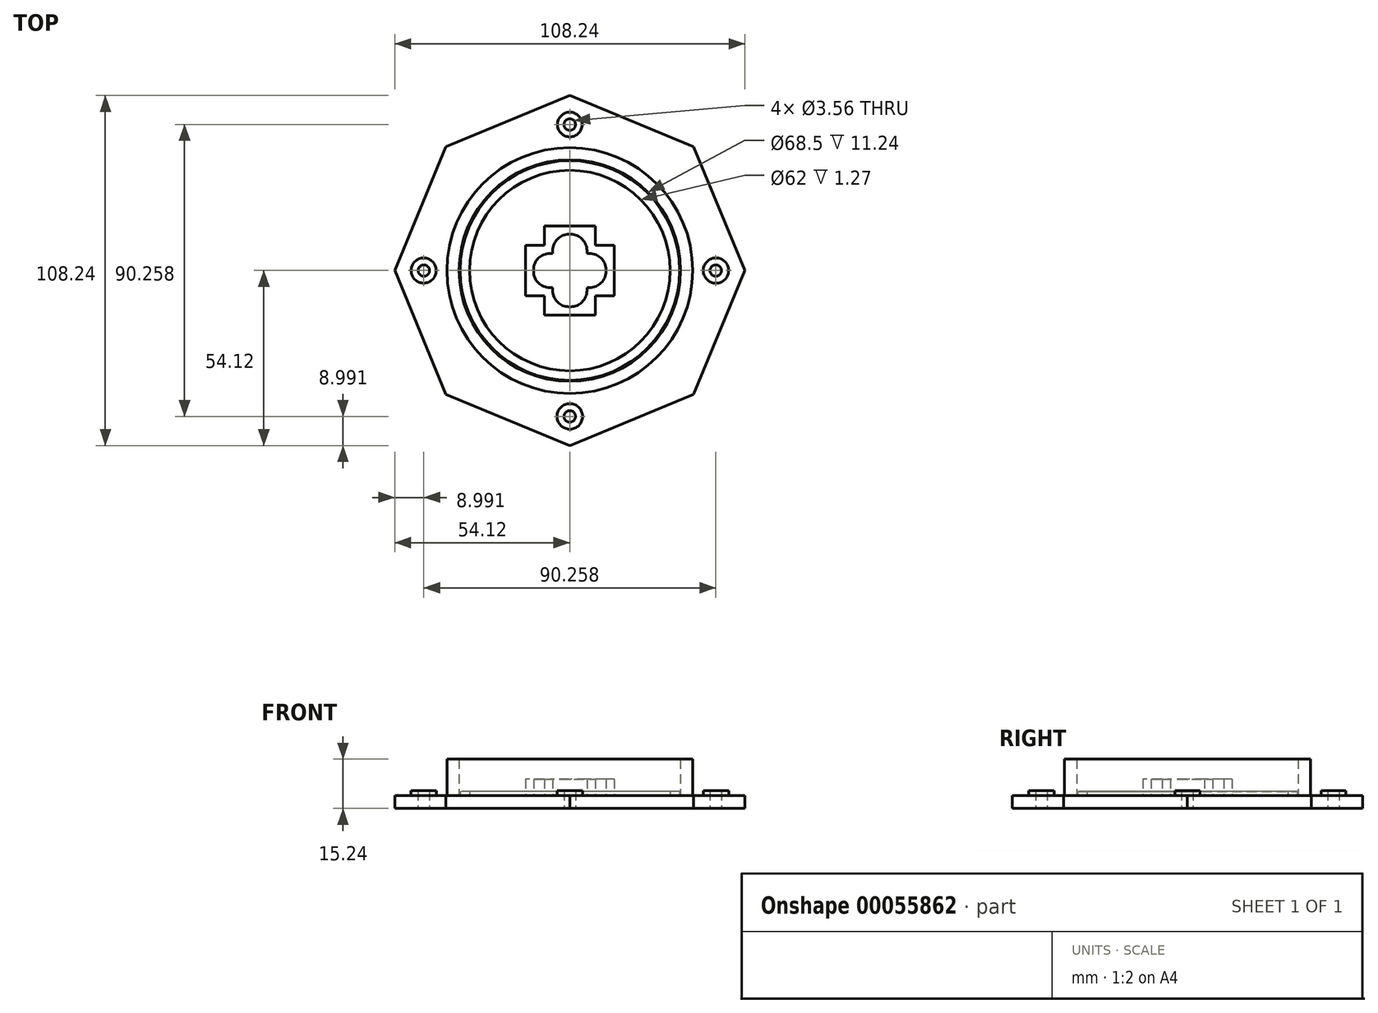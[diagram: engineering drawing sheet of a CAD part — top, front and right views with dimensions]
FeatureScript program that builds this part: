
annotation { "Feature Type Name" : "Feature", "Feature Type Description" : "" }
export const myFeature = defineFeature(function(context is Context, id is Id, definition is map)
    precondition{}
    {
        {
            var Q0;
            Q0=qCreatedBy(makeId("Top.planeOp"),FACE);
            var sketch = newSketch(context, id + "F0", { "sketchPlane" : qUnion([Q0])});
            skCircle(sketch, "E0.cCircle", {"center": v(0, 0) * mm, "radius": 54.12 * mm, "construction": true});
            skLineSegment(sketch, "E0.0", {"start": v(54.12, 0) * mm, "end": v(38.27, -38.27) * mm});
            skLineSegment(sketch, "E0.1", {"start": v(38.27, -38.27) * mm, "end": v(0, -54.12) * mm});
            skLineSegment(sketch, "E0.2", {"start": v(0, -54.12) * mm, "end": v(-38.27, -38.27) * mm});
            skLineSegment(sketch, "E0.3", {"start": v(-38.27, -38.27) * mm, "end": v(-54.12, 0) * mm});
            skLineSegment(sketch, "E0.4", {"start": v(-54.12, 0) * mm, "end": v(-38.27, 38.27) * mm});
            skLineSegment(sketch, "E0.5", {"start": v(-38.27, 38.27) * mm, "end": v(0, 54.12) * mm});
            skLineSegment(sketch, "E0.6", {"start": v(0, 54.12) * mm, "end": v(38.27, 38.27) * mm});
            skLineSegment(sketch, "E0.7", {"start": v(38.27, 38.27) * mm, "end": v(54.12, 0) * mm});
            skCircle(sketch, "E1", {"center": v(0, 45.13) * mm, "radius": 1.78 * mm});
            skCircle(sketch, "E2.1.0", {"center": v(-45.13, 0) * mm, "radius": 1.78 * mm});
            skCircle(sketch, "E2.2.0", {"center": v(0, -45.13) * mm, "radius": 1.78 * mm});
            skCircle(sketch, "E2.3.0", {"center": v(45.13, 0) * mm, "radius": 1.78 * mm});
            skSolve(sketch);
        }
        {
            var Q0;
            Q0 = qSketchRegion(id + "F0", true);
            extrude(context, id + "F1", {"entities" : qUnion([Q0]), "depth" : 4 * mm});
        }
        {
            var Q0;
            Q0=qCreatedBy(makeId("Top.planeOp"),FACE);
            var sketch = newSketch(context, id + "F2", { "sketchPlane" : qUnion([Q0])});
            skCircle(sketch, "E3", {"center": v(0, 0) * mm, "radius": 34.25 * mm});
            skCircle(sketch, "E4", {"center": v(0, 0) * mm, "radius": 38 * mm});
            skSolve(sketch);
        }
        {
            var Q0;
            Q0 = qSketchRegion(id + "F2", true);
            extrude(context, id + "F3", {"entities" : qUnion([Q0]), "operationType" : NewBodyOperationType.ADD, "depth" : 15.24 * mm});
        }
        {
            var Q0;
            {var subQ0=sQuery(id+"F0.wireOp",EDGE,"E0.3");var subQ1=sQuery(id+"F0.wireOp",EDGE,"E0.2");var subQ2=sQuery(id+"F0.wireOp",EDGE,"E0.1");var subQ3=sQuery(id+"F0.wireOp",EDGE,"E0.0");var subQ4=sQuery(id+"F0.wireOp",EDGE,"E0.4");var subQ5=sQuery(id+"F0.wireOp",EDGE,"E0.5");var subQ6=sQuery(id+"F0.wireOp",EDGE,"E0.6");var subQ7=sQuery(id+"F0.wireOp",EDGE,"E0.7");Q0=makeQuery(id+"F3.boolean.opBoolean","SPLIT",FACE,{"disambiguationData":[TD([makeQuery(id+"F1.opExtrude","SWEPT_FACE",FACE,{"disambiguationData":[OSD([subQ3])]})])],"derivedFrom":makeQuery(id+"F1.opExtrude","CAP_FACE",FACE,{"disambiguationData":[OSD([subQ3,subQ2,subQ1,subQ0,subQ4,subQ5,subQ6,subQ7])],"isStart":false})});}
            var sketch = newSketch(context, id + "F4", { "sketchPlane" : qUnion([Q0])});
            skCircle(sketch, "E5", {"center": v(0, 0) * mm, "radius": 31 * mm});
            skCircle(sketch, "E6", {"center": v(0, 0) * mm, "radius": 33.95 * mm});
            skSolve(sketch);
        }
        {
            var Q0;
            Q0 = qSketchRegion(id + "F4", true);
            extrude(context, id + "F5", {"entities" : qUnion([Q0]), "operationType" : NewBodyOperationType.ADD, "depth" : 1.27 * mm});
        }
        {
            var Q0;
            Q0=makeQuery(id+"F3.boolean.opBoolean","SPLIT",FACE,{"disambiguationData":[TD([makeQuery(id+"F3.opExtrude","SWEPT_FACE",FACE,{"disambiguationData":[OSD([sQuery(id+"F2.wireOp",EDGE,"E3")])]})])],"derivedFrom":makeQuery(id+"F1.opExtrude","CAP_FACE",FACE,{"disambiguationData":[OSD([sQuery(id+"F0.wireOp",EDGE,"E0.0"),sQuery(id+"F0.wireOp",EDGE,"E0.1"),sQuery(id+"F0.wireOp",EDGE,"E0.2"),sQuery(id+"F0.wireOp",EDGE,"E0.3"),sQuery(id+"F0.wireOp",EDGE,"E0.4"),sQuery(id+"F0.wireOp",EDGE,"E0.5"),sQuery(id+"F0.wireOp",EDGE,"E0.6"),sQuery(id+"F0.wireOp",EDGE,"E0.7")])],"isStart":false})});
            var sketch = newSketch(context, id + "F6", { "sketchPlane" : qUnion([Q0])});
            skLineSegment(sketch, "E7.rect.bottom", {"start": v(-0.22, 11.2) * mm, "end": v(0.22, 11.2) * mm});
            skLineSegment(sketch, "E7.rect.top", {"start": v(-0.22, -11.2) * mm, "end": v(0.22, -11.2) * mm});
            skLineSegment(sketch, "E7.rect.left", {"start": v(-5.3, 6.13) * mm, "end": v(-5.3, 5.3) * mm});
            skLineSegment(sketch, "E7.rect.right", {"start": v(5.3, 6.13) * mm, "end": v(5.3, 5.3) * mm});
            skPoint(sketch, "E7.rect.middle", {"position": v(0, 0) * mm});
            skLineSegment(sketch, "E8.rect.bottom", {"start": v(6.13, -5.3) * mm, "end": v(5.3, -5.3) * mm});
            skLineSegment(sketch, "E8.rect.top", {"start": v(6.13, 5.3) * mm, "end": v(5.3, 5.3) * mm});
            skLineSegment(sketch, "E8.rect.left", {"start": v(11.2, -0.22) * mm, "end": v(11.2, 0.22) * mm});
            skLineSegment(sketch, "E8.rect.right", {"start": v(-11.2, -0.22) * mm, "end": v(-11.2, 0.22) * mm});
            skLineSegment(sketch, "E9.trimOffspring", {"start": v(-5.3, -5.3) * mm, "end": v(-5.3, -6.13) * mm});
            skLineSegment(sketch, "E10.trimOffspring", {"start": v(5.3, -5.3) * mm, "end": v(5.3, -6.13) * mm});
            skLineSegment(sketch, "E11.trimOffspring", {"start": v(-5.3, 5.3) * mm, "end": v(-6.13, 5.3) * mm});
            skLineSegment(sketch, "E12.trimOffspring", {"start": v(-5.3, -5.3) * mm, "end": v(-6.13, -5.3) * mm});
            skLineSegment(sketch, "E13.0", {"start": v(-7.84, 13.75) * mm, "end": v(7.84, 13.75) * mm});
            skLineSegment(sketch, "E14.0", {"start": v(7.84, 11.12) * mm, "end": v(7.84, 7.84) * mm});
            skLineSegment(sketch, "E15.0", {"start": v(13.75, -7.84) * mm, "end": v(13.75, 7.84) * mm});
            skLineSegment(sketch, "E16.0", {"start": v(-7.84, -13.75) * mm, "end": v(7.84, -13.75) * mm});
            skLineSegment(sketch, "E17.0", {"start": v(-13.75, -7.84) * mm, "end": v(-13.75, 7.84) * mm});
            skLineSegment(sketch, "E18.0", {"start": v(-7.84, 7.84) * mm, "end": v(-11.3, 7.84) * mm});
            skLineSegment(sketch, "E19.0", {"start": v(-7.84, 11.3) * mm, "end": v(-7.84, 7.84) * mm});
            skLineSegment(sketch, "E20.0", {"start": v(11.12, 7.84) * mm, "end": v(7.84, 7.84) * mm});
            skLineSegment(sketch, "E21.0", {"start": v(11.3, -7.84) * mm, "end": v(7.84, -7.84) * mm});
            skLineSegment(sketch, "E22.0", {"start": v(7.84, -7.84) * mm, "end": v(7.84, -11.3) * mm});
            skLineSegment(sketch, "E23.0", {"start": v(-7.84, -7.84) * mm, "end": v(-7.84, -11.12) * mm});
            skLineSegment(sketch, "E24.0", {"start": v(-7.84, -7.84) * mm, "end": v(-11.12, -7.84) * mm});
            skLineSegment(sketch, "E25", {"start": v(-7.84, 11.3) * mm, "end": v(-7.84, 13.75) * mm});
            skLineSegment(sketch, "E26", {"start": v(7.84, 11.12) * mm, "end": v(7.84, 13.75) * mm});
            skLineSegment(sketch, "E27", {"start": v(-11.3, 7.84) * mm, "end": v(-13.75, 7.84) * mm});
            skLineSegment(sketch, "E28", {"start": v(-11.12, -7.84) * mm, "end": v(-13.75, -7.84) * mm});
            skLineSegment(sketch, "E29", {"start": v(-7.84, -11.12) * mm, "end": v(-7.84, -13.75) * mm});
            skLineSegment(sketch, "E30", {"start": v(7.84, -11.3) * mm, "end": v(7.84, -13.75) * mm});
            skLineSegment(sketch, "E31", {"start": v(11.3, -7.84) * mm, "end": v(13.75, -7.84) * mm});
            skLineSegment(sketch, "E32", {"start": v(11.12, 7.84) * mm, "end": v(13.75, 7.84) * mm});
            skPoint(sketch, "E33.visualSharp", {"position": v(5.3, 11.2) * mm});
            skArc(sketch, "E33.filletArc", {"start": v(5.3, 6.13) * mm, "mid": v(3.81, 9.72) * mm, "end": v(0.22, 11.2) * mm});
            skPoint(sketch, "E34.visualSharp", {"position": v(-5.3, 11.2) * mm});
            skArc(sketch, "E34.filletArc", {"start": v(-0.22, 11.2) * mm, "mid": v(-3.81, 9.72) * mm, "end": v(-5.3, 6.13) * mm});
            skPoint(sketch, "E35.visualSharp", {"position": v(-11.2, 5.3) * mm});
            skArc(sketch, "E35.filletArc", {"start": v(-6.13, 5.3) * mm, "mid": v(-9.72, 3.81) * mm, "end": v(-11.2, 0.22) * mm});
            skPoint(sketch, "E36.visualSharp", {"position": v(-11.2, -5.3) * mm});
            skArc(sketch, "E36.filletArc", {"start": v(-11.2, -0.22) * mm, "mid": v(-9.72, -3.81) * mm, "end": v(-6.13, -5.3) * mm});
            skPoint(sketch, "E37.visualSharp", {"position": v(-5.3, -11.2) * mm});
            skArc(sketch, "E37.filletArc", {"start": v(-5.3, -6.13) * mm, "mid": v(-3.81, -9.72) * mm, "end": v(-0.22, -11.2) * mm});
            skPoint(sketch, "E38.visualSharp", {"position": v(5.3, -11.2) * mm});
            skArc(sketch, "E38.filletArc", {"start": v(0.22, -11.2) * mm, "mid": v(3.81, -9.72) * mm, "end": v(5.3, -6.13) * mm});
            skPoint(sketch, "E39.visualSharp", {"position": v(11.2, -5.3) * mm});
            skArc(sketch, "E39.filletArc", {"start": v(6.13, -5.3) * mm, "mid": v(9.72, -3.81) * mm, "end": v(11.2, -0.22) * mm});
            skPoint(sketch, "E40.visualSharp", {"position": v(11.2, 5.3) * mm});
            skArc(sketch, "E40.filletArc", {"start": v(11.2, 0.22) * mm, "mid": v(9.72, 3.81) * mm, "end": v(6.13, 5.3) * mm});
            skSolve(sketch);
        }
        {
            var Q0;
            Q0 = qSketchRegion(id + "F6", true);
            extrude(context, id + "F7", {"entities" : qUnion([Q0]), "operationType" : NewBodyOperationType.ADD, "depth" : 5.08 * mm});
        }
        {
            var Q0;
            {var subQ4=sQuery(id+"F0.wireOp",EDGE,"E0.0");Q0=makeQuery(id+"F4.imprint","IMPRINT",FACE,{"disambiguationData":[TD([[makeQuery(id+"F4.imprint","IMPRINT",EDGE,{"derivedFrom":makeQuery(id+"F1.opExtrude","CAP_EDGE",EDGE,{"disambiguationData":[OSD([subQ4])],"isStart":false})}),-1.0]])]});}
            var sketch = newSketch(context, id + "F8", { "sketchPlane" : qUnion([Q0])});
            skCircle(sketch, "E41", {"center": v(0, 45.15) * mm, "radius": 3.81 * mm});
            skCircle(sketch, "E42", {"center": v(-45.18, 0) * mm, "radius": 3.88 * mm});
            skCircle(sketch, "E43", {"center": v(0, -45.12) * mm, "radius": 3.94 * mm});
            skCircle(sketch, "E44", {"center": v(45.2, 0) * mm, "radius": 3.93 * mm});
            skSolve(sketch);
        }
        {
            var Q0;
            Q0 = qSketchRegion(id + "F8", true);
            extrude(context, id + "F9", {"entities" : qUnion([Q0]), "operationType" : NewBodyOperationType.ADD, "depth" : 1.5 * mm});
        }
        {
            var Q0;
            Q0=makeQuery(id+"F1.opExtrude","CAP_FACE",FACE,{"disambiguationData":[OSD([sQuery(id+"F0.wireOp",EDGE,"E0.0"),sQuery(id+"F0.wireOp",EDGE,"E0.1"),sQuery(id+"F0.wireOp",EDGE,"E0.2"),sQuery(id+"F0.wireOp",EDGE,"E0.3"),sQuery(id+"F0.wireOp",EDGE,"E0.4"),sQuery(id+"F0.wireOp",EDGE,"E0.5"),sQuery(id+"F0.wireOp",EDGE,"E0.6"),sQuery(id+"F0.wireOp",EDGE,"E0.7"),sQuery(id+"F0.wireOp",EDGE,"E1"),sQuery(id+"F0.wireOp",EDGE,"E2.1.0"),sQuery(id+"F0.wireOp",EDGE,"E2.2.0"),sQuery(id+"F0.wireOp",EDGE,"E2.3.0")])],"isStart":true});
            var sketch = newSketch(context, id + "F10", { "sketchPlane" : qUnion([Q0])});
            skCircle(sketch, "E45", {"center": v(45.13, 0) * mm, "radius": 1.78 * mm});
            skCircle(sketch, "E46", {"center": v(0, -45.13) * mm, "radius": 1.78 * mm});
            skCircle(sketch, "E47", {"center": v(-45.13, 0) * mm, "radius": 1.78 * mm});
            skCircle(sketch, "E48", {"center": v(0, 45.13) * mm, "radius": 1.78 * mm});
            skSolve(sketch);
        }
        {
            var Q0;
            Q0 = qSketchRegion(id + "F10", true);
            extrude(context, id + "F11", {"entities" : qUnion([Q0]), "operationType" : NewBodyOperationType.REMOVE, "oppositeDirection" : true, "depth" : 25.4 * mm});
        }
    });
